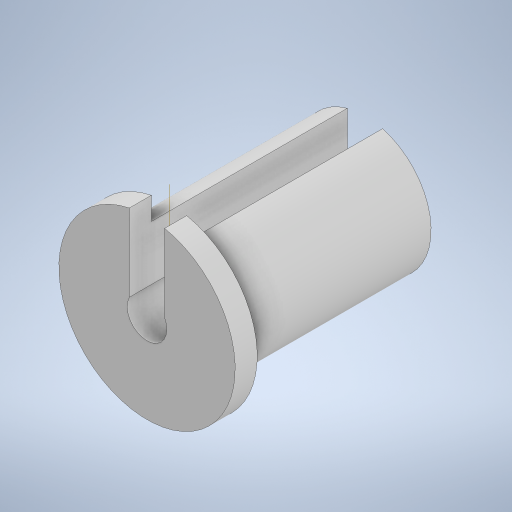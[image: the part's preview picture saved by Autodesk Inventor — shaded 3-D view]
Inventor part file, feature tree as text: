
AUTODESK INVENTOR PART (.ipt)
format: ipt  version: 2023 (Build 270158030, 158C)  size: 247,808 bytes
history: native  units: mm
features: extrude x4, sketch x4
ambient origin geometry x8: Origin, YZ Plane, XZ Plane, XY Plane, X Axis, Y Axis, Z Axis, Center Point
bodies: Solid1 (feature_tree)
feature tree (8):
  extrude  "Extrusion1"  Depth=5.0mm TaperAngle=0.0deg
  extrude  "Extrusion2"  Depth=44.45mm TaperAngle=0.0deg
  extrude  "Extrusion3"  TaperAngle=0.0deg  [1 undecoded]
  extrude  "Extrusion4"  TaperAngle=0.0deg  [1 undecoded]
  sketch  "Sketch1"  dims[d0=40.0mm d1=5.0mm d2=0.0mm]
  sketch  "Sketch2"  dims[d3=30.0mm d4=44.45mm d5=0.0mm]
  sketch  "Sketch3"  dims[d6=9.0mm d7=0.0mm d8=0.0mm]
  sketch  "Sketch4"  dims[d11=4.0mm d12=0.0mm d13=0.0mm]
note: 2 required parameter values undecoded (feature->parameter linkage not recoverable at this tier; creation-order binding heuristic only, values carry confidence <= 0.55)
